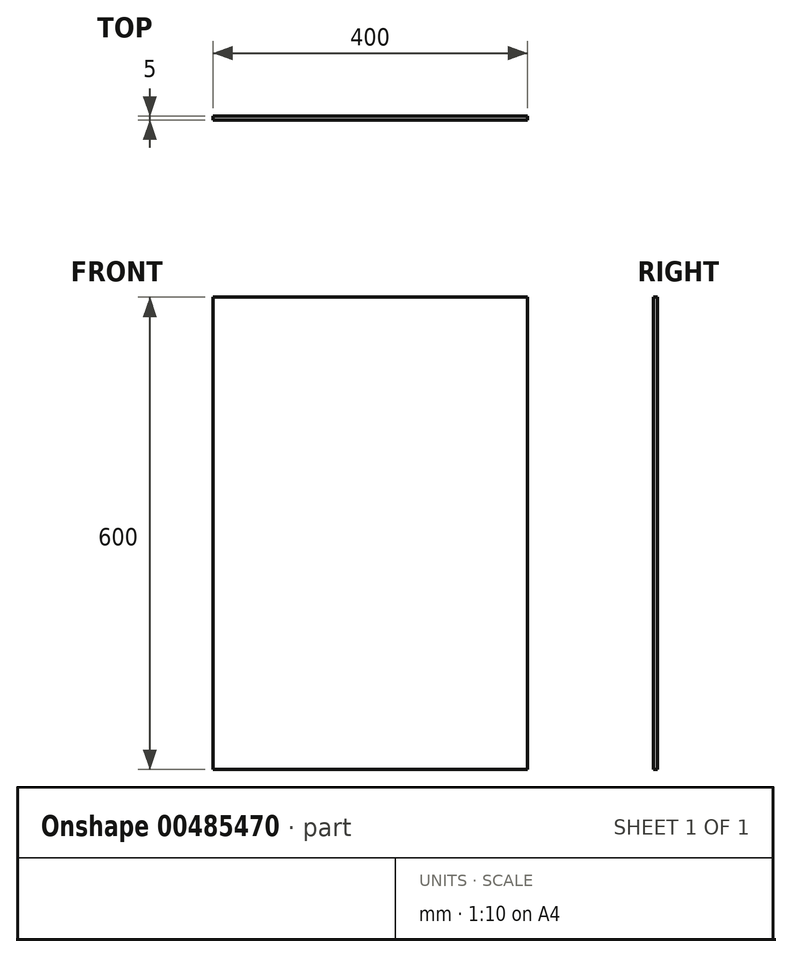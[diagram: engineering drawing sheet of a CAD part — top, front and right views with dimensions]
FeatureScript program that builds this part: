
annotation { "Feature Type Name" : "Feature", "Feature Type Description" : "" }
export const myFeature = defineFeature(function(context is Context, id is Id, definition is map)
    precondition{}
    {
        {
            var Q0;
            Q0=qCreatedBy(makeId("Front.planeOp"),FACE);
            var sketch = newSketch(context, id + "F0", { "sketchPlane" : qUnion([Q0])});
            skLineSegment(sketch, "E0.bottom", {"start": v(-198.52, 195.3) * mm, "end": v(201.48, 195.3) * mm});
            skLineSegment(sketch, "E0.top", {"start": v(-198.52, -404.7) * mm, "end": v(201.48, -404.7) * mm});
            skLineSegment(sketch, "E0.left", {"start": v(-198.52, 195.3) * mm, "end": v(-198.52, -404.7) * mm});
            skLineSegment(sketch, "E0.right", {"start": v(201.48, 195.3) * mm, "end": v(201.48, -404.7) * mm});
            skSolve(sketch);
        }
        {
            var Q0;
            Q0 = qSketchRegion(id + "F0", true);
            extrude(context, id + "F1", {"entities" : qUnion([Q0]), "depth" : 5 * mm});
        }
    });
